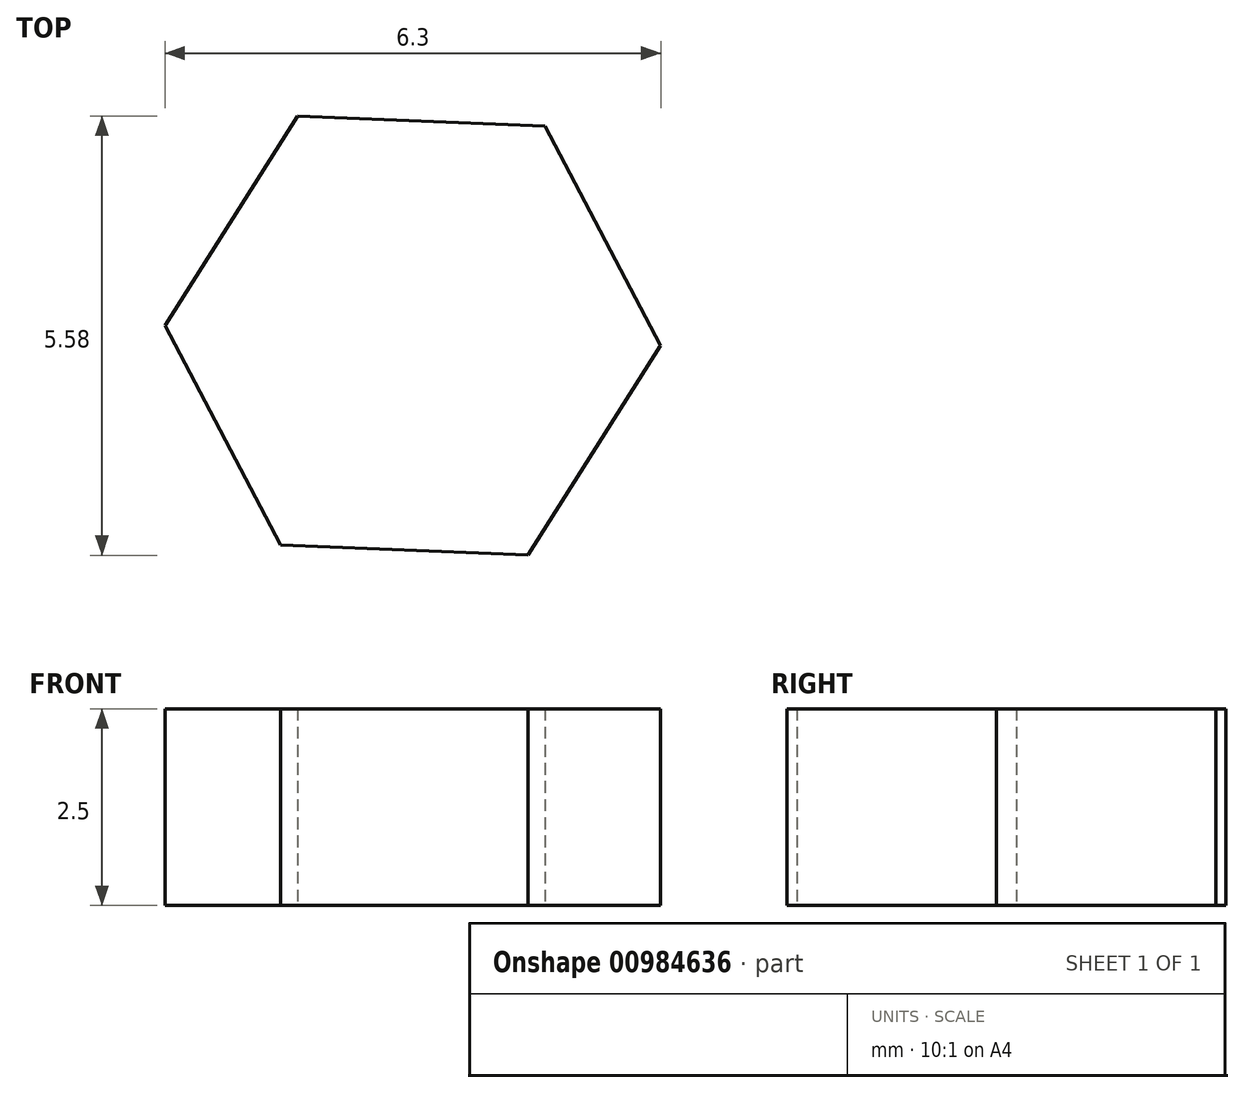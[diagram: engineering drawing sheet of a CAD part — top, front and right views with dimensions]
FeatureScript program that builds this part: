
annotation { "Feature Type Name" : "Feature", "Feature Type Description" : "" }
export const myFeature = defineFeature(function(context is Context, id is Id, definition is map)
    precondition{}
    {
        {
            var Q0;
            Q0=qCreatedBy(makeId("Top.planeOp"),FACE);
            var sketch = newSketch(context, id + "F0", { "sketchPlane" : qUnion([Q0])});
            skCircle(sketch, "E0.cCircle", {"center": v(0, 0) * mm, "radius": 2.73 * mm, "construction": true});
            skLineSegment(sketch, "E0.0", {"start": v(3.15, -0.13) * mm, "end": v(1.46, -2.79) * mm});
            skLineSegment(sketch, "E0.1", {"start": v(1.46, -2.79) * mm, "end": v(-1.68, -2.66) * mm});
            skLineSegment(sketch, "E0.2", {"start": v(-1.68, -2.66) * mm, "end": v(-3.15, 0.13) * mm});
            skLineSegment(sketch, "E0.3", {"start": v(-3.15, 0.13) * mm, "end": v(-1.46, 2.79) * mm});
            skLineSegment(sketch, "E0.4", {"start": v(-1.46, 2.79) * mm, "end": v(1.68, 2.66) * mm});
            skLineSegment(sketch, "E0.5", {"start": v(1.68, 2.66) * mm, "end": v(3.15, -0.13) * mm});
            skPoint(sketch, "E0.0.midPoint", {"position": v(2.3, -1.46) * mm});
            skSolve(sketch);
        }
        {
            var Q0;
            Q0 = qSketchRegion(id + "F0", true);
            extrude(context, id + "F1", {"entities" : qUnion([Q0]), "depth" : 2.5 * mm, "offsetDistance" : 25 * mm});
        }
    });
